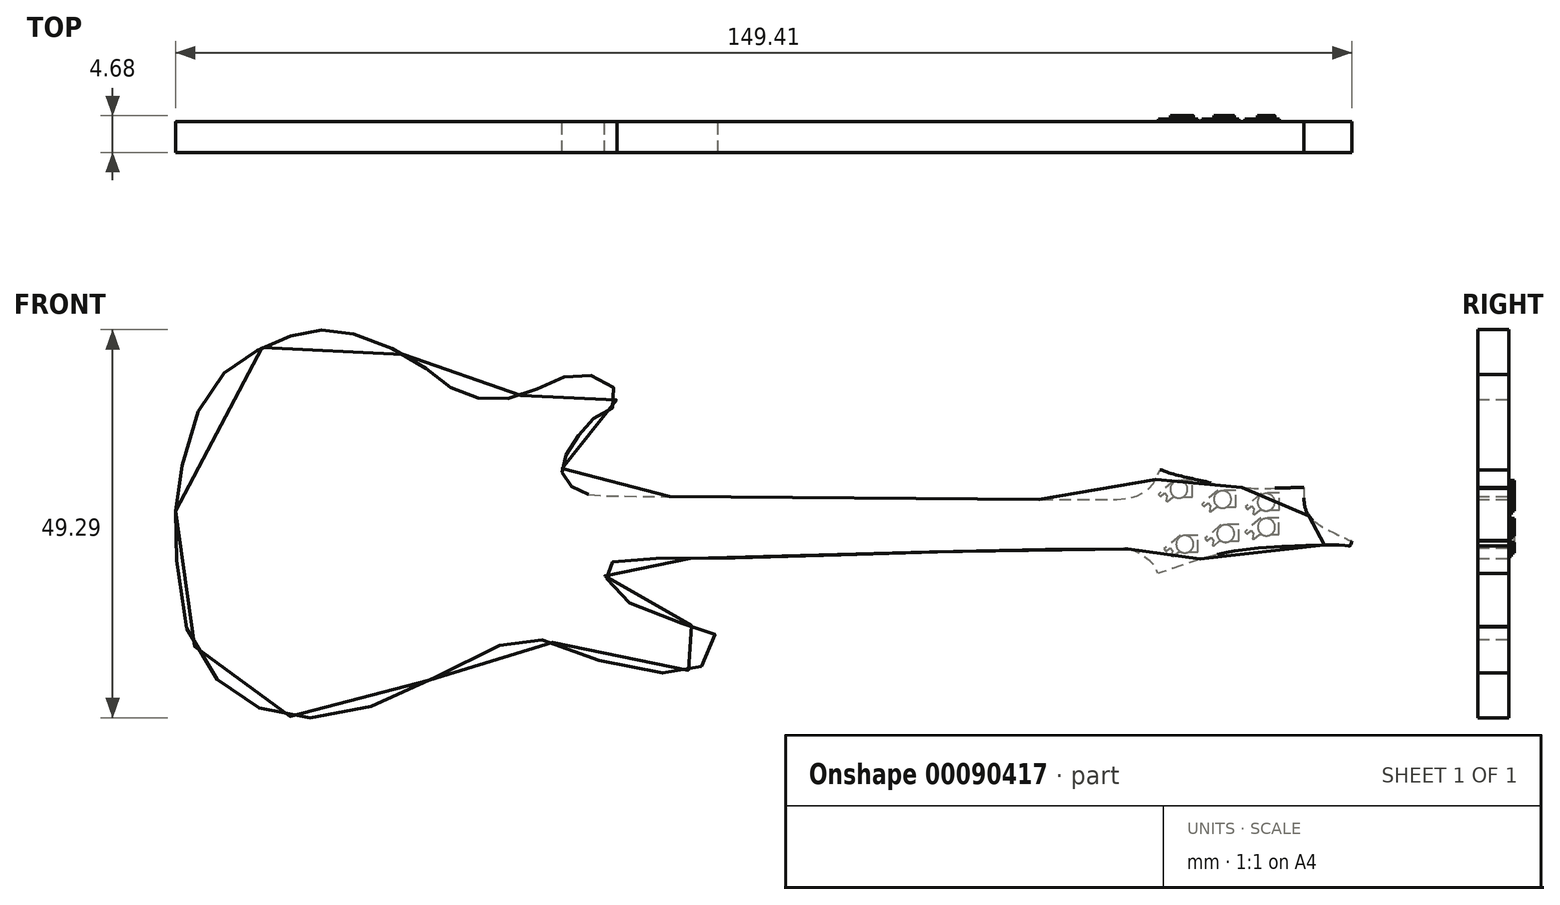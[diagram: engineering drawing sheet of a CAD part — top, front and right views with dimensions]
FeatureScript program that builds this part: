
annotation { "Feature Type Name" : "Feature", "Feature Type Description" : "" }
export const myFeature = defineFeature(function(context is Context, id is Id, definition is map)
    precondition{}
    {
        {
            var Q0;
            Q0=qCreatedBy(makeId("Front.planeOp"),FACE);
            var sketch = newSketch(context, id + "F0", { "sketchPlane" : qUnion([Q0])});
            skFitSpline(sketch, "E0", {"points": [v(-74.37, 1.64) * mm, v(-70.9, 15.67) * mm, v(-63.82, 22.18) * mm, v(-57.45, 24.5) * mm, v(-52.1, 24.2) * mm, v(-43.57, 20.44) * mm, v(-39.09, 17.12) * mm, v(-34.46, 15.82) * mm, v(-29.55, 16.68) * mm, v(-24.92, 18.7) * mm, v(-21.01, 18.7) * mm, v(-18.41, 16.68) * mm, v(-19.28, 14.37) * mm, v(-21.6, 13.21) * mm, v(-23.47, 10.9) * mm, v(-24.92, 8.44) * mm, v(-25.3, 6.74) * mm, v(-24.8, 5.56) * mm, v(-23.21, 4.15) * mm, v(-21.07, 3.65) * mm, v(-3.35, 3.5) * mm, v(40.27, 3.1) * mm, v(46.95, 3.35) * mm, v(48.34, 3.85) * mm, v(49.24, 4.5) * mm, v(50.1, 5.67) * mm, v(50.64, 6.86) * mm, v(51.32, 6.67) * mm, v(54.92, 5.72) * mm, v(58.77, 4.9) * mm, v(63.45, 4.53) * mm, v(68.84, 4.67) * mm, v(68.92, 4.64) * mm, v(68.95, 4.48) * mm, v(68.95, 4.29) * mm, v(69, 2.44) * mm, v(69.55, 1.06) * mm, v(70.71, 0) * mm, v(74.97, -2.13) * mm, v(74.99, -2.11) * mm, v(75, -2.27) * mm, v(74.93, -2.52) * mm, v(74.78, -2.76) * mm, v(74.47, -2.75) * mm, v(70.67, -2.7) * mm, v(67.74, -2.8) * mm, v(62.7, -3.1) * mm, v(56, -4.39) * mm, v(50.54, -6.24) * mm, v(50.37, -6.24) * mm, v(50.24, -5.94) * mm, v(49.68, -5) * mm, v(48.26, -3.92) * mm, v(46.71, -3.23) * mm, v(37.21, -3.23) * mm, v(22.3, -3.53) * mm, v(0.45, -4.26) * mm, v(-11.84, -4.35) * mm, v(-17.78, -4.52) * mm, v(-18.78, -4.78) * mm, v(-19.42, -5.06) * mm, v(-19.8, -5.65) * mm, v(-19.9, -6.49) * mm, v(-19.5, -7.08) * mm, v(-18.63, -8.02) * mm, v(-16.76, -10) * mm, v(-13.03, -11.83) * mm, v(-7.48, -13.08) * mm, v(-7.28, -13.03) * mm, v(-5.82, -14.08) * mm, v(-5.76, -15.88) * mm, v(-7.7, -18.13) * mm, v(-9.04, -18.56) * mm, v(-12.93, -18.92) * mm, v(-20.05, -17.52) * mm, v(-26.74, -14.97) * mm, v(-29.65, -14.67) * mm, v(-33.12, -15.4) * mm, v(-40.96, -19.23) * mm, v(-48.8, -22.93) * mm, v(-55.74, -24.52) * mm, v(-60.54, -24.33) * mm, v(-65.04, -22.81) * mm, v(-68.57, -20.32) * mm, v(-71.85, -15.82) * mm, v(-74.04, -8.77) * mm, v(-74.28, -1.6) * mm, v(-74.37, 1.64) * mm]});
            skSolve(sketch);
        }
        {
            var Q0;
            Q0=makeQuery(id+"F0.imprint","IMPRINT",FACE,{"disambiguationData":[TD([[makeQuery(id+"F0.imprint","IMPRINT",EDGE,{"derivedFrom":sQuery(id+"F0.wireOp",EDGE,"E0")}),-1.0]])]});
            extrude(context, id + "F1", {"entities" : qUnion([Q0]), "depth" : 3.93 * mm});
        }
        {
            var Q0;
            Q0=qCreatedBy(makeId("Front.planeOp"),FACE);
            var sketch = newSketch(context, id + "F2", { "sketchPlane" : qUnion([Q0])});
            skCircle(sketch, "E1", {"center": v(53.05, 4.4) * mm, "radius": 1.1 * mm});
            skCircle(sketch, "E2", {"center": v(58.6, 3.13) * mm, "radius": 1.1 * mm});
            skCircle(sketch, "E3", {"center": v(64.13, 2.76) * mm, "radius": 1.1 * mm});
            skCircle(sketch, "E4", {"center": v(64.17, -0.4) * mm, "radius": 1.1 * mm});
            skCircle(sketch, "E5", {"center": v(58.98, -1.22) * mm, "radius": 1.1 * mm});
            skCircle(sketch, "E6", {"center": v(53.8, -2.57) * mm, "radius": 1.1 * mm});
            skSolve(sketch);
        }
        {
            var Q0;
            Q0=makeQuery(id+"F2.imprint","IMPRINT",FACE,{"disambiguationData":[TD([[makeQuery(id+"F2.imprint","IMPRINT",EDGE,{"derivedFrom":sQuery(id+"F2.wireOp",EDGE,"E3")}),1.0]])]});
            var Q1;
            Q1=makeQuery(id+"F2.imprint","IMPRINT",FACE,{"disambiguationData":[TD([[makeQuery(id+"F2.imprint","IMPRINT",EDGE,{"derivedFrom":sQuery(id+"F2.wireOp",EDGE,"E2")}),1.0]])]});
            var Q2;
            Q2=makeQuery(id+"F2.imprint","IMPRINT",FACE,{"disambiguationData":[TD([[makeQuery(id+"F2.imprint","IMPRINT",EDGE,{"derivedFrom":sQuery(id+"F2.wireOp",EDGE,"E1")}),1.0]])]});
            var Q3;
            Q3=makeQuery(id+"F2.imprint","IMPRINT",FACE,{"disambiguationData":[TD([[makeQuery(id+"F2.imprint","IMPRINT",EDGE,{"derivedFrom":sQuery(id+"F2.wireOp",EDGE,"E6")}),1.0]])]});
            var Q4;
            Q4=makeQuery(id+"F2.imprint","IMPRINT",FACE,{"disambiguationData":[TD([[makeQuery(id+"F2.imprint","IMPRINT",EDGE,{"derivedFrom":sQuery(id+"F2.wireOp",EDGE,"E5")}),1.0]])]});
            var Q5;
            Q5=makeQuery(id+"F2.imprint","IMPRINT",FACE,{"disambiguationData":[TD([[makeQuery(id+"F2.imprint","IMPRINT",EDGE,{"derivedFrom":sQuery(id+"F2.wireOp",EDGE,"E4")}),1.0]])]});
            extrude(context, id + "F3", {"entities" : qUnion([Q0, Q1, Q2, Q3, Q4, Q5]), "operationType" : NewBodyOperationType.ADD, "oppositeDirection" : true, "depth" : 0.75 * mm});
        }
        {
            var Q0;
            Q0=qCreatedBy(makeId("Front.planeOp"),FACE);
            var sketch = newSketch(context, id + "F4", { "sketchPlane" : qUnion([Q0])});
            skLineSegment(sketch, "E7", {"start": v(65.82, 1.81) * mm, "end": v(65.82, 3.92) * mm});
            skLineSegment(sketch, "E8", {"start": v(65.82, 3.92) * mm, "end": v(63.55, 3.92) * mm});
            skLineSegment(sketch, "E9", {"start": v(63.55, 3.92) * mm, "end": v(61.48, 2.14) * mm});
            skLineSegment(sketch, "E10", {"start": v(61.48, 2.14) * mm, "end": v(61.72, 1.86) * mm});
            skLineSegment(sketch, "E11", {"start": v(61.72, 1.86) * mm, "end": v(62.24, 2.31) * mm});
            skLineSegment(sketch, "E12", {"start": v(62.24, 2.31) * mm, "end": v(62.57, 1.93) * mm});
            skLineSegment(sketch, "E13", {"start": v(62.57, 1.93) * mm, "end": v(62.45, 1.26) * mm});
            skLineSegment(sketch, "E14", {"start": v(62.45, 1.26) * mm, "end": v(62.61, 1.23) * mm});
            skLineSegment(sketch, "E15", {"start": v(62.61, 1.23) * mm, "end": v(63.35, 1.81) * mm});
            skLineSegment(sketch, "E16", {"start": v(63.35, 1.81) * mm, "end": v(65.82, 1.81) * mm});
            skLineSegment(sketch, "E17", {"start": v(60.3, 2.17) * mm, "end": v(60.3, 4.27) * mm});
            skLineSegment(sketch, "E18", {"start": v(60.3, 4.27) * mm, "end": v(58.02, 4.27) * mm});
            skLineSegment(sketch, "E19", {"start": v(58.02, 4.27) * mm, "end": v(55.95, 2.5) * mm});
            skLineSegment(sketch, "E20", {"start": v(55.95, 2.5) * mm, "end": v(56.2, 2.22) * mm});
            skLineSegment(sketch, "E21", {"start": v(56.2, 2.22) * mm, "end": v(56.71, 2.67) * mm});
            skLineSegment(sketch, "E22", {"start": v(56.71, 2.67) * mm, "end": v(57.05, 2.28) * mm});
            skLineSegment(sketch, "E23", {"start": v(57.05, 2.28) * mm, "end": v(56.92, 1.62) * mm});
            skLineSegment(sketch, "E24", {"start": v(56.92, 1.62) * mm, "end": v(57.08, 1.58) * mm});
            skLineSegment(sketch, "E25", {"start": v(57.08, 1.58) * mm, "end": v(57.82, 2.17) * mm});
            skLineSegment(sketch, "E26", {"start": v(57.82, 2.17) * mm, "end": v(60.3, 2.17) * mm});
            skLineSegment(sketch, "E27", {"start": v(54.77, 3.45) * mm, "end": v(54.77, 5.56) * mm});
            skLineSegment(sketch, "E28", {"start": v(54.77, 5.56) * mm, "end": v(52.5, 5.56) * mm});
            skLineSegment(sketch, "E29", {"start": v(52.5, 5.56) * mm, "end": v(50.43, 3.78) * mm});
            skLineSegment(sketch, "E30", {"start": v(50.43, 3.78) * mm, "end": v(50.67, 3.5) * mm});
            skLineSegment(sketch, "E31", {"start": v(50.67, 3.5) * mm, "end": v(51.2, 3.95) * mm});
            skLineSegment(sketch, "E32", {"start": v(51.2, 3.95) * mm, "end": v(51.52, 3.56) * mm});
            skLineSegment(sketch, "E33", {"start": v(51.52, 3.56) * mm, "end": v(51.4, 2.9) * mm});
            skLineSegment(sketch, "E34", {"start": v(51.4, 2.9) * mm, "end": v(51.56, 2.87) * mm});
            skLineSegment(sketch, "E35", {"start": v(51.56, 2.87) * mm, "end": v(52.3, 3.45) * mm});
            skLineSegment(sketch, "E36", {"start": v(52.3, 3.45) * mm, "end": v(54.77, 3.45) * mm});
            skLineSegment(sketch, "E37", {"start": v(65.76, -1.33) * mm, "end": v(65.76, 0.78) * mm});
            skLineSegment(sketch, "E38", {"start": v(65.76, 0.78) * mm, "end": v(63.48, 0.78) * mm});
            skLineSegment(sketch, "E39", {"start": v(63.48, 0.78) * mm, "end": v(61.41, -1) * mm});
            skLineSegment(sketch, "E40", {"start": v(61.41, -1) * mm, "end": v(61.65, -1.28) * mm});
            skLineSegment(sketch, "E41", {"start": v(61.65, -1.28) * mm, "end": v(62.18, -0.83) * mm});
            skLineSegment(sketch, "E42", {"start": v(62.18, -0.83) * mm, "end": v(62.5, -1.22) * mm});
            skLineSegment(sketch, "E43", {"start": v(62.5, -1.22) * mm, "end": v(62.38, -1.88) * mm});
            skLineSegment(sketch, "E44", {"start": v(62.38, -1.88) * mm, "end": v(62.55, -1.91) * mm});
            skLineSegment(sketch, "E45", {"start": v(62.55, -1.91) * mm, "end": v(63.28, -1.33) * mm});
            skLineSegment(sketch, "E46", {"start": v(63.28, -1.33) * mm, "end": v(65.76, -1.33) * mm});
            skLineSegment(sketch, "E47", {"start": v(60.69, -2.18) * mm, "end": v(60.69, -0.07) * mm});
            skLineSegment(sketch, "E48", {"start": v(60.69, -0.07) * mm, "end": v(58.41, -0.07) * mm});
            skLineSegment(sketch, "E49", {"start": v(58.41, -0.07) * mm, "end": v(56.34, -1.85) * mm});
            skLineSegment(sketch, "E50", {"start": v(56.34, -1.85) * mm, "end": v(56.59, -2.13) * mm});
            skLineSegment(sketch, "E51", {"start": v(56.59, -2.13) * mm, "end": v(57.1, -1.68) * mm});
            skLineSegment(sketch, "E52", {"start": v(57.1, -1.68) * mm, "end": v(57.44, -2.07) * mm});
            skLineSegment(sketch, "E53", {"start": v(57.44, -2.07) * mm, "end": v(57.31, -2.73) * mm});
            skLineSegment(sketch, "E54", {"start": v(57.31, -2.73) * mm, "end": v(57.48, -2.76) * mm});
            skLineSegment(sketch, "E55", {"start": v(57.48, -2.76) * mm, "end": v(58.21, -2.18) * mm});
            skLineSegment(sketch, "E56", {"start": v(58.21, -2.18) * mm, "end": v(60.69, -2.18) * mm});
            skLineSegment(sketch, "E57", {"start": v(55.49, -3.53) * mm, "end": v(55.49, -1.42) * mm});
            skLineSegment(sketch, "E58", {"start": v(55.49, -1.42) * mm, "end": v(53.21, -1.42) * mm});
            skLineSegment(sketch, "E59", {"start": v(53.21, -1.42) * mm, "end": v(51.14, -3.2) * mm});
            skLineSegment(sketch, "E60", {"start": v(51.14, -3.2) * mm, "end": v(51.38, -3.48) * mm});
            skLineSegment(sketch, "E61", {"start": v(51.38, -3.48) * mm, "end": v(51.9, -3.03) * mm});
            skLineSegment(sketch, "E62", {"start": v(51.9, -3.03) * mm, "end": v(52.24, -3.42) * mm});
            skLineSegment(sketch, "E63", {"start": v(52.24, -3.42) * mm, "end": v(52.11, -4.08) * mm});
            skLineSegment(sketch, "E64", {"start": v(52.11, -4.08) * mm, "end": v(52.28, -4.11) * mm});
            skLineSegment(sketch, "E65", {"start": v(52.28, -4.11) * mm, "end": v(53.01, -3.53) * mm});
            skLineSegment(sketch, "E66", {"start": v(53.01, -3.53) * mm, "end": v(55.49, -3.53) * mm});
            skSolve(sketch);
        }
        {
            var Q0;
            Q0=makeQuery(id+"F4.imprint","IMPRINT",FACE,{"disambiguationData":[TD([[makeQuery(id+"F4.imprint","IMPRINT",EDGE,{"derivedFrom":sQuery(id+"F4.wireOp",EDGE,"E7")}),1.0]])]});
            var Q1;
            Q1=makeQuery(id+"F4.imprint","IMPRINT",FACE,{"disambiguationData":[TD([[makeQuery(id+"F4.imprint","IMPRINT",EDGE,{"derivedFrom":sQuery(id+"F4.wireOp",EDGE,"E17")}),1.0]])]});
            var Q2;
            Q2=makeQuery(id+"F4.imprint","IMPRINT",FACE,{"disambiguationData":[TD([[makeQuery(id+"F4.imprint","IMPRINT",EDGE,{"derivedFrom":sQuery(id+"F4.wireOp",EDGE,"E27")}),1.0]])]});
            var Q3;
            Q3=makeQuery(id+"F4.imprint","IMPRINT",FACE,{"disambiguationData":[TD([[makeQuery(id+"F4.imprint","IMPRINT",EDGE,{"derivedFrom":sQuery(id+"F4.wireOp",EDGE,"E57")}),1.0]])]});
            var Q4;
            Q4=makeQuery(id+"F4.imprint","IMPRINT",FACE,{"disambiguationData":[TD([[makeQuery(id+"F4.imprint","IMPRINT",EDGE,{"derivedFrom":sQuery(id+"F4.wireOp",EDGE,"E47")}),1.0]])]});
            var Q5;
            Q5=makeQuery(id+"F4.imprint","IMPRINT",FACE,{"disambiguationData":[TD([[makeQuery(id+"F4.imprint","IMPRINT",EDGE,{"derivedFrom":sQuery(id+"F4.wireOp",EDGE,"E37")}),1.0]])]});
            extrude(context, id + "F5", {"entities" : qUnion([Q0, Q1, Q2, Q3, Q4, Q5]), "operationType" : NewBodyOperationType.ADD, "oppositeDirection" : true, "depth" : 0.33 * mm});
        }
        {
            var Q0;
            Q0=qCreatedBy(makeId("Right.planeOp"),FACE);
            cPlane(context, id + "F6", {"entities" : qUnion([Q0]), "cplaneType" : CPlaneType.OFFSET, "offset" : 47 * mm, "width" : 150 * mm, "height" : 150 * mm});
        }
    });
